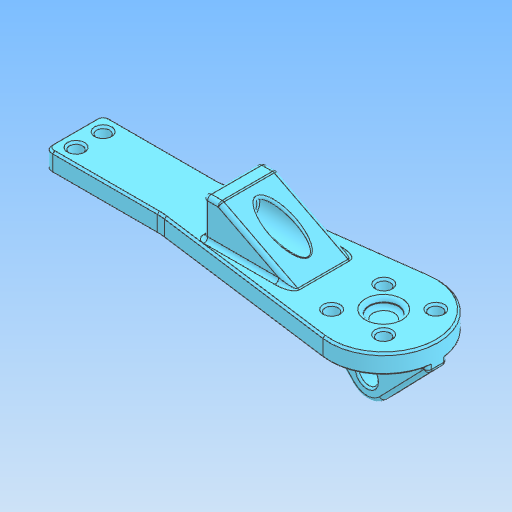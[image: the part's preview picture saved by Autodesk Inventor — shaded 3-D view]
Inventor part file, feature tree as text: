
AUTODESK INVENTOR PART (.ipt)
format: ipt  version: 2021.2 (Build 252289000, 289)  size: 705,536 bytes
history: native  units: mm
features: fillet x8, other x4, chamfer x2
ambient origin geometry x8: Origin, YZ Plane, XZ Plane, XY Plane, X Axis, Y Axis, Z Axis, Center Point
bodies: Body1 (feature_tree)
feature tree (14):
  other  "Твёрдое тело.ipt"
  fillet  "Сопряжение1"  Radius=10.0mm
  chamfer  "Фаска1"  Distance=2.0mm
  chamfer  "Фаска2"  Distance=0.5mm Angle=45.0deg
  fillet  "Сопряжение2"  Radius=0.5mm
  fillet  "Сопряжение3"  Radius=1.0mm
  fillet  "Сопряжение9"  Radius=1.0mm
  fillet  "Сопряжение5"  Radius=1.0mm
  fillet  "Сопряжение6"  Radius=0.5mm
  fillet  "Сопряжение7"  Radius=1.0mm
  fillet  "Сопряжение8"  Radius=0.5mm
  other  "Ложечка::Твёрдое тело.ipt"
  other  "Элемент создания тегов1"
  other  "Твердое тело1"
